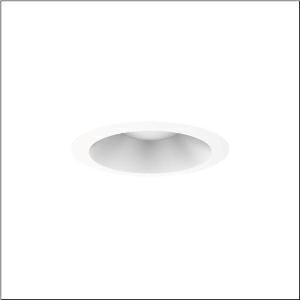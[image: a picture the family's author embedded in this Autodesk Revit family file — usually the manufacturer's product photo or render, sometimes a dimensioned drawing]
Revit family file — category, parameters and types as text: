
# Revit family: lunis_31_midi_51dn167g32
name_source: partatom
category: Lighting Fixtures
units: mm (PartAtom-declared; Revit-internal decimal feet)

## family parameters
Cut with Voids When Loaded = No
Host = Face
Light Source = No
Part Type = Normal
Room Calculation Point = No
Round Connector Dimension = Use Diameter
Shared = No

## types (1)
- Lunis 31 midi (1 x LED, 2000 lm, 17 W, 3000K)
    Apparent Load = 17 VA
    CIE Flux Codes = 64 93 99 100 100
    Color Rendering = 80
    Color Temperature = 3000K
    Default Elevation = 1800 mm
    Description = Lunis 31,  midi, downlight, light control with reflector, light emission: direct distribution, LED rated luminous flux: 2.000lm, light colour: 830, mains connection: 220..240V, AC, 50/60Hz, housing, white, protection rating (complete): IP20, protection rating (on room side): IP54, insulation class (complete): insulation class II (safety insulation), certification: CE, packaging unit: 1 piece
    Height = 0 mm  [stored 0 ft]
    Lamp = 1 x LED
    Lamp Light Flux = 2000 lm
    Lamp Power = 17 W
    Lamp count = 1
    Length = 259 mm
    Luminous efficacy = 118 lm/W
    Manufacturer = Siteco
    ModVariant = No
    Model = 51DN167G32
    Mounting Place = Ceiling
    Mounting Type = Recessed
    Number of Poles = 1
    OnlyDefault = Yes
    Power Factor = 1
    Product Name = Lunis 31 midi
    Product group = downlight
    ProductGroupID = 400
    Protection Class = Protection class II
    Protection Degree = IP 20
    RLX_Detail_Level = 1
    RLX_Emergency_Light_Flux = 0 lm
    RLX_Emergency_Type = 0
    RLX_Emergency_Type_DB = No
    RlxData = <blob elided: 23661 chars, md5=77cd872c>
    Socket = socket
    Standby Power = 0 W
    System Light Flux = 2000 lm
    System Power = 17 W
    Type Comments = Product without accessories
    Type Image = l_1006711.jpg
    URL = http://relux.com
    VarID = ---
    Voltage = 0 V
    Weight = 0.00 kg
    Width = 0 mm  [stored 0 ft]

note: [stored X ft] marks values corroborated as IEEE doubles in the binary element streams (Revit-internal decimal feet)

## geometry (parser evidence)
native form markers: Blend x4, Sweep x10
no freeform markers — native parametric forms only
